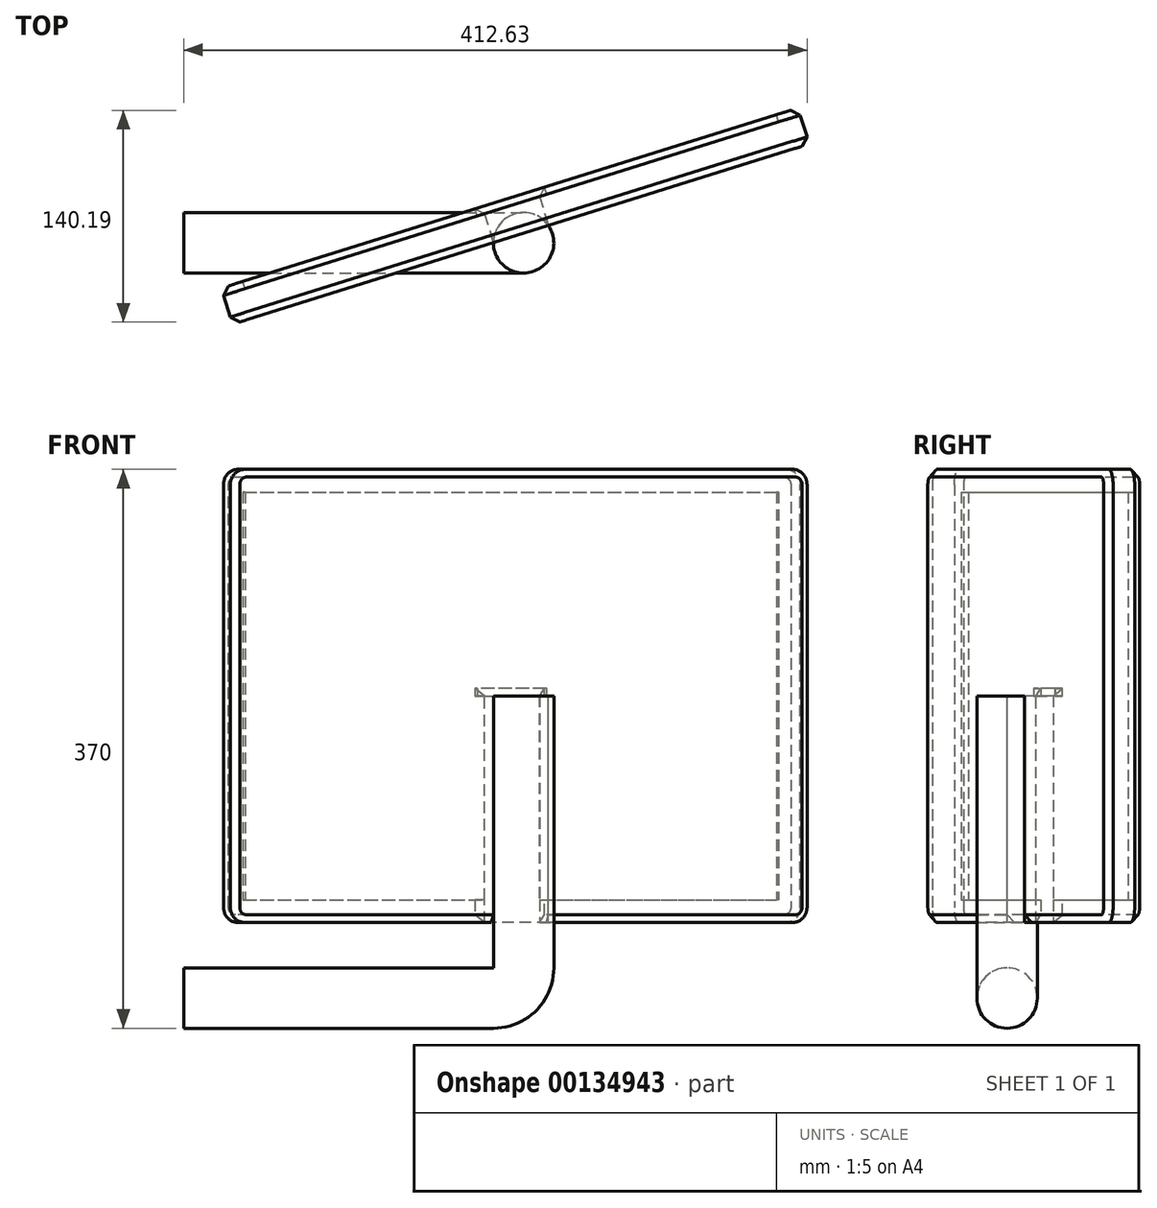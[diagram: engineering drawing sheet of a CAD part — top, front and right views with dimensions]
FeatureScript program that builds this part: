
annotation { "Feature Type Name" : "Feature", "Feature Type Description" : "" }
export const myFeature = defineFeature(function(context is Context, id is Id, definition is map)
    precondition{}
    {
        {
            var Q0;
            Q0=qCreatedBy(makeId("Front.planeOp"),FACE);
            var sketch = newSketch(context, id + "F0", { "sketchPlane" : qUnion([Q0])});
            skLineSegment(sketch, "E0", {"start": v(0, 0) * mm, "end": v(130, 0) * mm});
            skLineSegment(sketch, "E1", {"start": v(150, 20) * mm, "end": v(150, 200) * mm});
            skPoint(sketch, "E2.visualSharp", {"position": v(150, 0) * mm});
            skArc(sketch, "E2.filletArc", {"start": v(130, 0) * mm, "mid": v(144.14, 5.86) * mm, "end": v(150, 20) * mm});
            skSolve(sketch);
        }
        {
            var Q0;
            Q0=qCreatedBy(makeId("Right.planeOp"),FACE);
            var sketch = newSketch(context, id + "F1", { "sketchPlane" : qUnion([Q0])});
            skCircle(sketch, "E3", {"center": v(0, 0) * mm, "radius": 20 * mm});
            skSolve(sketch);
        }
        {
            var Q0;
            Q0=makeQuery(id+"F1.imprint","IMPRINT",FACE,{"disambiguationData":[TD([[makeQuery(id+"F1.imprint","IMPRINT",EDGE,{"derivedFrom":sQuery(id+"F1.wireOp",EDGE,"E3")}),1.0]])]});
            var Q1;
            Q1=sQuery(id+"F0.wireOp",EDGE,"E1");
            var Q2;
            Q2=sQuery(id+"F0.wireOp",EDGE,"E2.filletArc");
            var Q3;
            Q3=sQuery(id+"F0.wireOp",EDGE,"E0");
            sweep(context, id + "F2", {"profiles" : qUnion([Q0]), "path" : qUnion([Q1, Q2, Q3])});
        }
        {
            var Q0;
            Q0=makeQuery(id+"F2.opSweep","CAP_FACE",FACE,{"disambiguationData":[OSD([sQuery(id+"F0.wireOp",VERTEX,"E1.end"),sQuery(id+"F1.wireOp",EDGE,"E3")])],"isStart":false});
            var sketch = newSketch(context, id + "F3", { "sketchPlane" : qUnion([Q0])});
            skLineSegment(sketch, "E4", {"start": v(150, 0) * mm, "end": v(170, 0) * mm});
            skLineSegment(sketch, "E5", {"start": v(170, 0) * mm, "end": v(130, 0) * mm});
            skLineSegment(sketch, "E6.top", {"start": v(170, 25) * mm, "end": v(130, 25) * mm});
            skLineSegment(sketch, "E6.left", {"start": v(170, 0) * mm, "end": v(170, 25) * mm});
            skLineSegment(sketch, "E6.right", {"start": v(130, 0) * mm, "end": v(130, 25) * mm});
            skLineSegment(sketch, "E7", {"start": v(170, 25) * mm, "end": v(130, 0) * mm, "construction": true});
            skLineSegment(sketch, "E8", {"start": v(170, 12.5) * mm, "end": v(130, 0) * mm});
            skSolve(sketch);
        }
        {
            var Q0;
            Q0=makeQuery(id+"F3.imprint","IMPRINT",FACE,{"disambiguationData":[TD([[makeQuery(id+"F3.imprint","IMPRINT",EDGE,{"derivedFrom":sQuery(id+"F3.wireOp",EDGE,"E6.top")}),1.0]])]});
            var Q1;
            {var subQ0=sQuery(id+"F3.wireOp",EDGE,"E8");var subQ1=makeQuery(id+"F2.opSweep","CAP_EDGE",EDGE,{"disambiguationData":[OSD([sQuery(id+"F0.wireOp",VERTEX,"E1.end"),sQuery(id+"F1.wireOp",EDGE,"E3")])],"isStart":false});var subQ3=makeQuery(id+"F3.imprint","INTERSECT",VERTEX,{"derivedFrom":[subQ1,subQ0]});Q1=makeQuery(id+"F3.imprint","IMPRINT",FACE,{"disambiguationData":[TD([[makeQuery(id+"F3.imprint","IMPRINT",EDGE,{"disambiguationData":[TD([[subQ3,-1.0]])],"derivedFrom":subQ0}),-1.0]])]});}
            extrude(context, id + "F4", {"entities" : qUnion([Q0, Q1]), "operationType" : NewBodyOperationType.REMOVE, "oppositeDirection" : true, "depth" : 150 * mm});
        }
        {
            var Q0;
            Q0=makeQuery(id+"F4.boolean.opBoolean","COPY",FACE,{"derivedFrom":makeQuery(id+"F4.opExtrude","SWEPT_FACE",FACE,{"disambiguationData":[OSD([sQuery(id+"F3.wireOp",EDGE,"E8")])]})});
            var sketch = newSketch(context, id + "F5", { "sketchPlane" : qUnion([Q0])});
            skLineSegment(sketch, "E9.bottom", {"start": v(56.83, 50) * mm, "end": v(-343.17, 50) * mm});
            skLineSegment(sketch, "E9.top", {"start": v(56.83, 350) * mm, "end": v(-343.17, 350) * mm});
            skLineSegment(sketch, "E9.left", {"start": v(56.83, 50) * mm, "end": v(56.83, 350) * mm});
            skLineSegment(sketch, "E9.right", {"start": v(-343.17, 50) * mm, "end": v(-343.17, 350) * mm});
            skPoint(sketch, "E9.middle", {"position": v(-143.17, 200) * mm});
            skSolve(sketch);
        }
        {
            var Q0;
            Q0=makeQuery(id+"F5.imprint","IMPRINT",FACE,{"disambiguationData":[TD([[makeQuery(id+"F5.imprint","IMPRINT",EDGE,{"derivedFrom":sQuery(id+"F5.wireOp",EDGE,"E9.top")}),1.0]])]});
            var Q1;
            {var subQ1=sQuery(id+"F3.wireOp",EDGE,"E5");Q1=makeQuery(id+"F5.imprint","IMPRINT",FACE,{"disambiguationData":[TD([[makeQuery(id+"F5.imprint","IMPRINT",EDGE,{"derivedFrom":makeQuery(id+"F4.boolean.opBoolean","COPY",EDGE,{"derivedFrom":makeQuery(id+"F4.opExtrude","CAP_EDGE",EDGE,{"disambiguationData":[OSD([subQ1])],"isStart":true})})}),-1.0]])]});}
            var Q2;
            {var subQ1=sQuery(id+"F3.wireOp",EDGE,"E8");Q2=makeQuery(id+"F5.imprint","IMPRINT",FACE,{"disambiguationData":[TD([[makeQuery(id+"F5.imprint","IMPRINT",EDGE,{"derivedFrom":makeQuery(id+"F4.boolean.opBoolean","COPY",EDGE,{"derivedFrom":makeQuery(id+"F4.opExtrude","CAP_EDGE",EDGE,{"disambiguationData":[OSD([subQ1])],"isStart":true})})}),-1.0]])]});}
            extrude(context, id + "F6", {"entities" : qUnion([Q0, Q1, Q2]), "operationType" : NewBodyOperationType.ADD, "depth" : 25 * mm});
        }
        {
            var Q0;
            Q0=makeQuery(id+"F2.opSweep","CAP_FACE",FACE,{"disambiguationData":[OSD([sQuery(id+"F0.wireOp",VERTEX,"E0.start"),sQuery(id+"F1.wireOp",EDGE,"E3")])],"isStart":true});
            extrude(context, id + "F7", {"entities" : qUnion([Q0]), "operationType" : NewBodyOperationType.ADD, "depth" : 75 * mm});
        }
        {
            var Q0;
            Q0=makeQuery(id+"F6.opExtrude","SWEPT_EDGE",EDGE,{"disambiguationData":[OSD([sQuery(id+"F5.wireOp",EDGE,"E9.top"),sQuery(id+"F5.wireOp",EDGE,"E9.right")])]});
            var Q1;
            Q1=makeQuery(id+"F6.opExtrude","SWEPT_EDGE",EDGE,{"disambiguationData":[OSD([sQuery(id+"F5.wireOp",EDGE,"E9.top"),sQuery(id+"F5.wireOp",EDGE,"E9.left")])]});
            var Q2;
            Q2=makeQuery(id+"F6.opExtrude","SWEPT_EDGE",EDGE,{"disambiguationData":[OSD([sQuery(id+"F5.wireOp",EDGE,"E9.bottom"),sQuery(id+"F5.wireOp",EDGE,"E9.right")])]});
            var Q3;
            Q3=makeQuery(id+"F6.opExtrude","SWEPT_EDGE",EDGE,{"disambiguationData":[OSD([sQuery(id+"F5.wireOp",EDGE,"E9.bottom"),sQuery(id+"F5.wireOp",EDGE,"E9.left")])]});
            fillet(context, id + "F8", {"entities" : qUnion([Q0, Q1, Q2, Q3]), "radius" : 10 * mm, "tangentPropagation" : true, "allowEdgeOverflow" : false});
        }
        {
            var Q0;
            {var subQ0=sQuery(id+"F5.wireOp",EDGE,"E9.bottom");var subQ1=sQuery(id+"F5.wireOp",EDGE,"E9.right");Q0=makeQuery(id+"F6.boolean.opBoolean","SPLIT",EDGE,{"disambiguationData":[TD([makeQuery(id+"F6.opExtrude","SWEPT_FACE",FACE,{"disambiguationData":[OSD([subQ1])]})])],"derivedFrom":makeQuery(id+"F6.opExtrude","CAP_EDGE",EDGE,{"disambiguationData":[OSD([subQ0])],"isStart":true})});}
            var Q1;
            Q1=makeQuery(id+"F6.opExtrude","CAP_FACE",FACE,{"disambiguationData":[OSD([sQuery(id+"F5.wireOp",EDGE,"E9.bottom"),sQuery(id+"F5.wireOp",EDGE,"E9.top"),sQuery(id+"F5.wireOp",EDGE,"E9.left"),sQuery(id+"F5.wireOp",EDGE,"E9.right")])],"isStart":false});
            chamfer(context, id + "F9", {"entities" : qUnion([Q0, Q1]), "width" : 5 * mm, "tangentPropagation" : true});
        }
        {
            var Q0;
            Q0=makeQuery(id+"F6.opExtrude","CAP_FACE",FACE,{"disambiguationData":[OSD([sQuery(id+"F5.wireOp",EDGE,"E9.bottom"),sQuery(id+"F5.wireOp",EDGE,"E9.top"),sQuery(id+"F5.wireOp",EDGE,"E9.left"),sQuery(id+"F5.wireOp",EDGE,"E9.right")])],"isStart":false});
            var sketch = newSketch(context, id + "F10", { "sketchPlane" : qUnion([Q0])});
            skLineSegment(sketch, "E10", {"start": v(-338.17, 200) * mm, "end": v(51.83, 200) * mm});
            skLineSegment(sketch, "E11.bottom", {"start": v(41.83, 335) * mm, "end": v(-328.17, 335) * mm});
            skLineSegment(sketch, "E11.top", {"start": v(41.83, 65) * mm, "end": v(-328.17, 65) * mm});
            skLineSegment(sketch, "E11.left", {"start": v(41.83, 335) * mm, "end": v(41.83, 65) * mm});
            skLineSegment(sketch, "E11.right", {"start": v(-328.17, 335) * mm, "end": v(-328.17, 65) * mm});
            skPoint(sketch, "E11.middle", {"position": v(-143.17, 200) * mm});
            skSolve(sketch);
        }
        {
            var Q0;
            {var subQ5=sQuery(id+"F10.wireOp",EDGE,"E11.bottom");Q0=makeQuery(id+"F10.imprint","IMPRINT",FACE,{"disambiguationData":[TD([[makeQuery(id+"F10.imprint","IMPRINT",EDGE,{"derivedFrom":subQ5}),1.0]])]});}
            var Q1;
            {var subQ5=sQuery(id+"F10.wireOp",EDGE,"E11.top");Q1=makeQuery(id+"F10.imprint","IMPRINT",FACE,{"disambiguationData":[TD([[makeQuery(id+"F10.imprint","IMPRINT",EDGE,{"derivedFrom":subQ5}),-1.0]])]});}
            extrude(context, id + "F11", {"entities" : qUnion([Q0, Q1]), "operationType" : NewBodyOperationType.REMOVE, "oppositeDirection" : true, "depth" : 5 * mm});
        }
        {
            var Q0;
            Q0=makeQuery(id+"F11.boolean.opBoolean","COPY",FACE,{"derivedFrom":makeQuery(id+"F11.opExtrude","CAP_FACE",FACE,{"disambiguationData":[OSD([sQuery(id+"F10.wireOp",EDGE,"E11.bottom"),sQuery(id+"F10.wireOp",EDGE,"E11.top"),sQuery(id+"F10.wireOp",EDGE,"E11.left"),sQuery(id+"F10.wireOp",EDGE,"E11.right")])],"isStart":false})});
            extrude(context, id + "F12", {"entities" : qUnion([Q0]), "depth" : .1 * mm});
        }
    });
